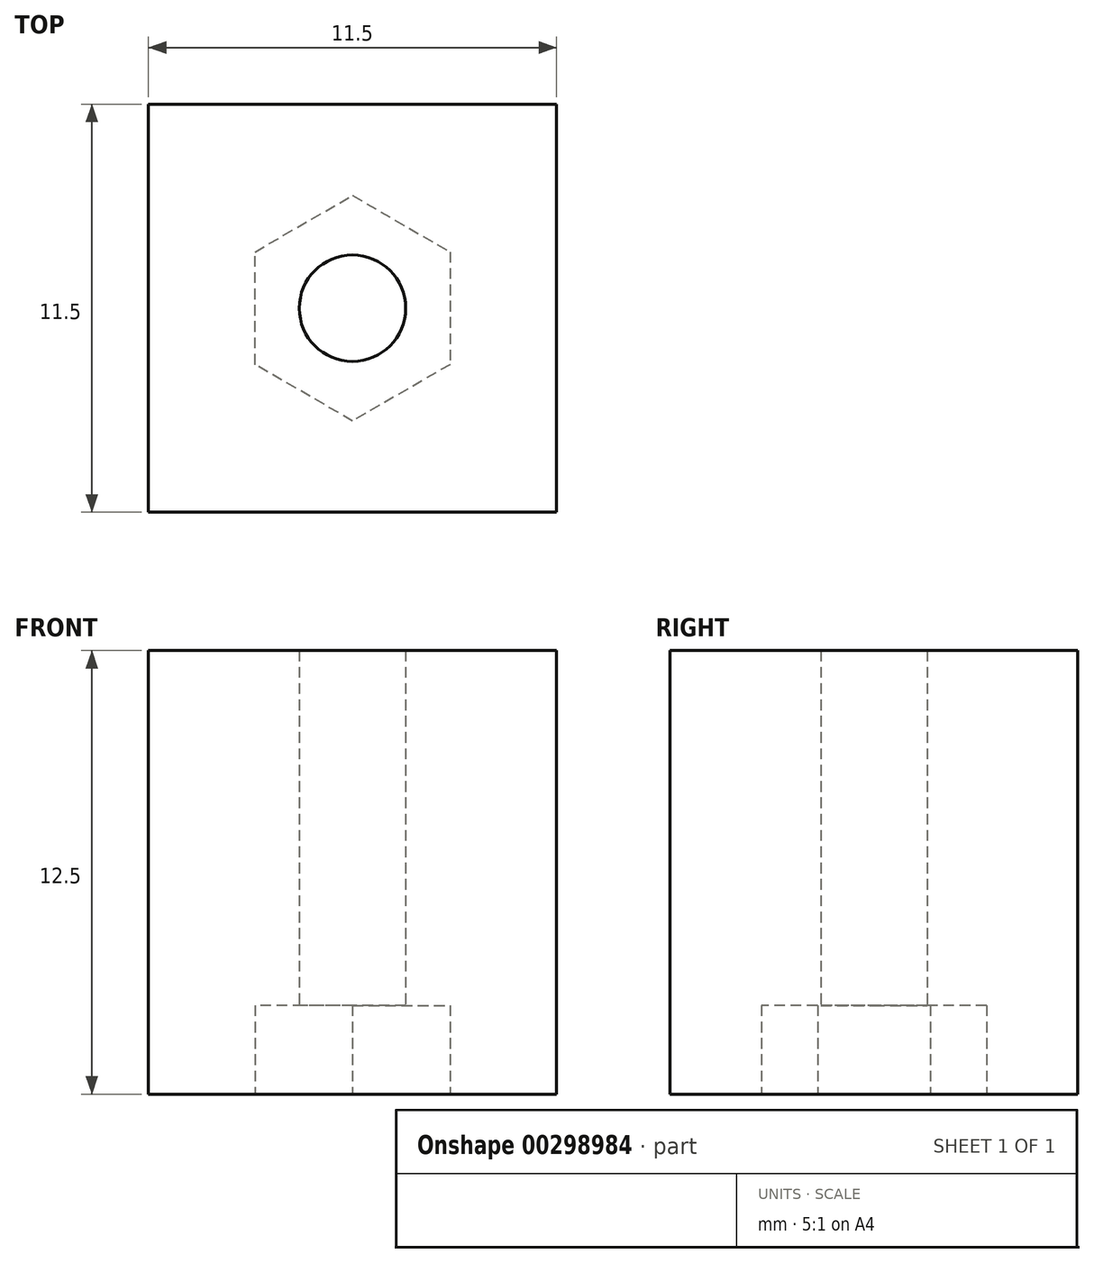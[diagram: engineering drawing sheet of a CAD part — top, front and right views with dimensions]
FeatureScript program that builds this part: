
annotation { "Feature Type Name" : "Feature", "Feature Type Description" : "" }
export const myFeature = defineFeature(function(context is Context, id is Id, definition is map)
    precondition{}
    {
        {
            var Q0;
            Q0=qCreatedBy(makeId("Top.planeOp"),FACE);
            var sketch = newSketch(context, id + "F0", { "sketchPlane" : qUnion([Q0])});
            skCircle(sketch, "E0.cCircle", {"center": v(0, 0) * mm, "radius": 2.75 * mm, "construction": true});
            skLineSegment(sketch, "E0.0", {"start": v(2.75, 1.59) * mm, "end": v(2.75, -1.59) * mm});
            skLineSegment(sketch, "E0.1", {"start": v(2.75, -1.59) * mm, "end": v(0, -3.18) * mm});
            skLineSegment(sketch, "E0.2", {"start": v(0, -3.18) * mm, "end": v(-2.75, -1.59) * mm});
            skLineSegment(sketch, "E0.3", {"start": v(-2.75, -1.59) * mm, "end": v(-2.75, 1.59) * mm});
            skLineSegment(sketch, "E0.4", {"start": v(-2.75, 1.59) * mm, "end": v(0, 3.18) * mm});
            skLineSegment(sketch, "E0.5", {"start": v(0, 3.18) * mm, "end": v(2.75, 1.59) * mm});
            skPoint(sketch, "E0.0.midPoint", {"position": v(2.75, 0) * mm});
            skLineSegment(sketch, "E1.bottom", {"start": v(-5.75, 5.75) * mm, "end": v(5.75, 5.75) * mm});
            skLineSegment(sketch, "E1.top", {"start": v(-5.75, -5.75) * mm, "end": v(5.75, -5.75) * mm});
            skLineSegment(sketch, "E1.left", {"start": v(-5.75, 5.75) * mm, "end": v(-5.75, -5.75) * mm});
            skLineSegment(sketch, "E1.right", {"start": v(5.75, 5.75) * mm, "end": v(5.75, -5.75) * mm});
            skSolve(sketch);
        }
        {
            var Q0;
            Q0 = qSketchRegion(id + "F0", true);
            extrude(context, id + "F1", {"entities" : qUnion([Q0]), "depth" : 2.5 * mm});
        }
        {
            var Q0;
            Q0=makeQuery(id+"F1.opExtrude","CAP_FACE",FACE,{"disambiguationData":[OSD([sQuery(id+"F0.wireOp",EDGE,"E0.0"),sQuery(id+"F0.wireOp",EDGE,"E0.1"),sQuery(id+"F0.wireOp",EDGE,"E0.2"),sQuery(id+"F0.wireOp",EDGE,"E0.3"),sQuery(id+"F0.wireOp",EDGE,"E0.4"),sQuery(id+"F0.wireOp",EDGE,"E0.5"),sQuery(id+"F0.wireOp",EDGE,"E1.bottom"),sQuery(id+"F0.wireOp",EDGE,"E1.top"),sQuery(id+"F0.wireOp",EDGE,"E1.left"),sQuery(id+"F0.wireOp",EDGE,"E1.right")])],"isStart":false});
            var sketch = newSketch(context, id + "F2", { "sketchPlane" : qUnion([Q0])});
            skLineSegment(sketch, "E2.0", {"start": v(-5.75, 5.75) * mm, "end": v(5.75, 5.75) * mm});
            skLineSegment(sketch, "E3.0", {"start": v(5.75, 5.75) * mm, "end": v(5.75, -5.75) * mm});
            skLineSegment(sketch, "E4.0", {"start": v(-5.75, -5.75) * mm, "end": v(5.75, -5.75) * mm});
            skLineSegment(sketch, "E5.0", {"start": v(-5.75, 5.75) * mm, "end": v(-5.75, -5.75) * mm});
            skCircle(sketch, "E6", {"center": v(0, 0) * mm, "radius": 1.5 * mm});
            skSolve(sketch);
        }
        {
            var Q0;
            Q0 = qSketchRegion(id + "F2", true);
            extrude(context, id + "F3", {"entities" : qUnion([Q0]), "operationType" : NewBodyOperationType.ADD, "depth" : 10 * mm});
        }
    });
